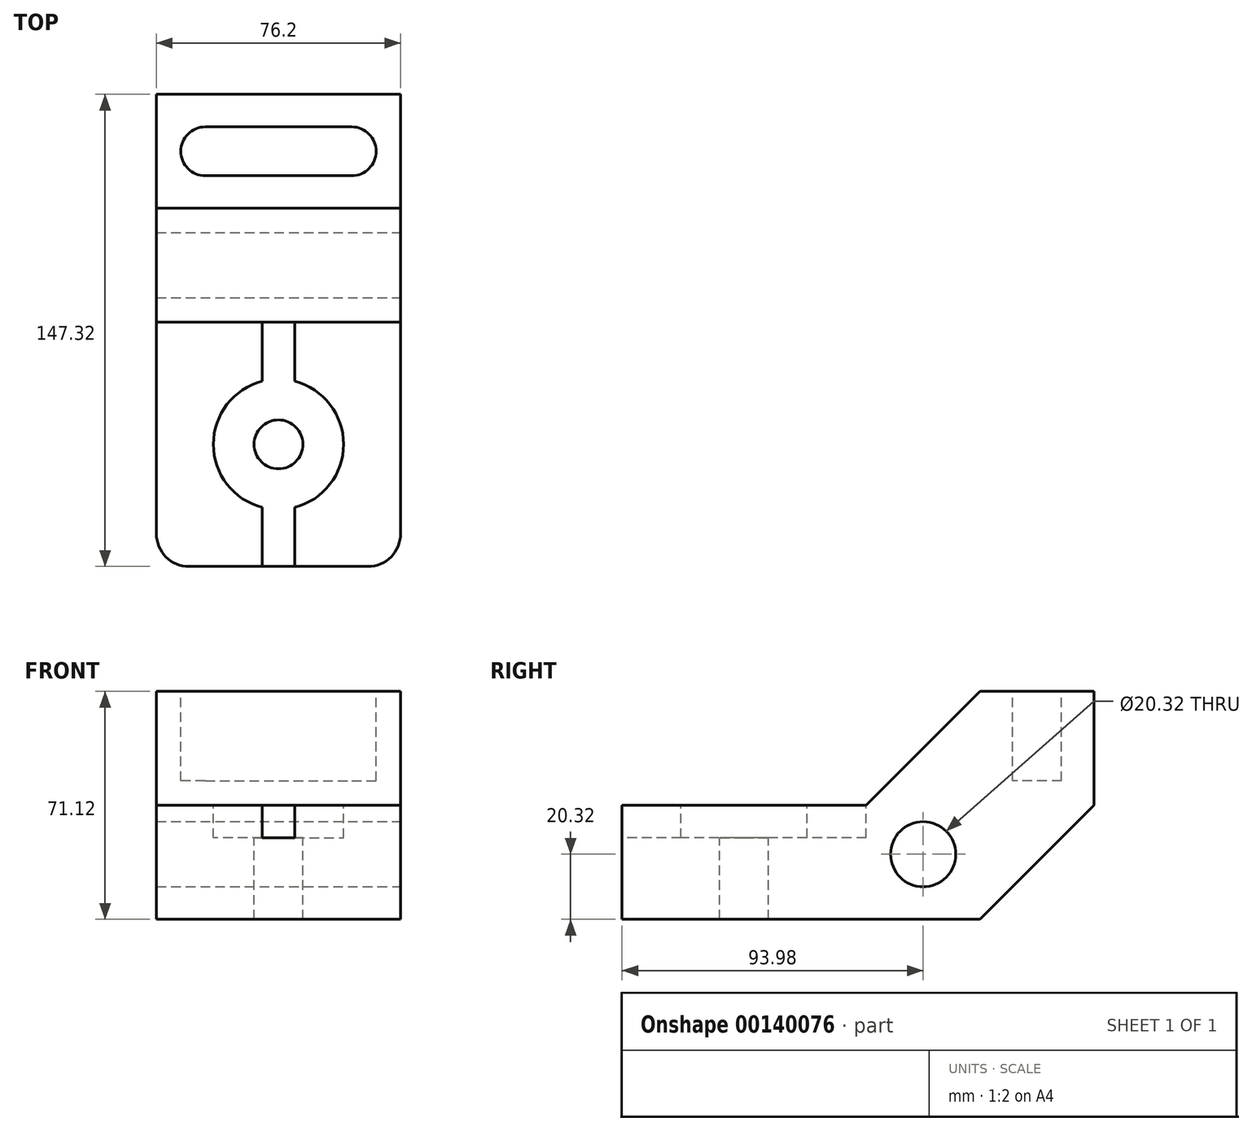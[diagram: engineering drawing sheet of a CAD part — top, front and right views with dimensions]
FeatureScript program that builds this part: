
annotation { "Feature Type Name" : "Feature", "Feature Type Description" : "" }
export const myFeature = defineFeature(function(context is Context, id is Id, definition is map)
    precondition{}
    {
        {
            var Q0;
            Q0=qCreatedBy(makeId("Right.planeOp"),FACE);
            var sketch = newSketch(context, id + "F0", { "sketchPlane" : qUnion([Q0])});
            skLineSegment(sketch, "E0", {"start": v(0, 0) * mm, "end": v(111.76, 0) * mm});
            skLineSegment(sketch, "E1", {"start": v(111.76, 0) * mm, "end": v(147.32, 35.56) * mm});
            skLineSegment(sketch, "E2", {"start": v(147.32, 35.56) * mm, "end": v(147.32, 71.12) * mm});
            skLineSegment(sketch, "E3", {"start": v(147.32, 71.12) * mm, "end": v(111.76, 71.12) * mm});
            skLineSegment(sketch, "E4", {"start": v(111.76, 71.12) * mm, "end": v(76.2, 35.56) * mm});
            skLineSegment(sketch, "E5", {"start": v(76.2, 35.56) * mm, "end": v(0, 35.56) * mm});
            skLineSegment(sketch, "E6", {"start": v(0, 35.56) * mm, "end": v(0, 0) * mm});
            skSolve(sketch);
        }
        {
            var Q0;
            Q0 = qSketchRegion(id + "F0", true);
            extrude(context, id + "F1", {"entities" : qUnion([Q0]), "endBound" : BoundingType.SYMMETRIC, "depth" : 76.2 * mm});
        }
        {
            var Q0;
            Q0=makeQuery(id+"F1.opExtrude","CAP_EDGE",EDGE,{"disambiguationData":[OSD([sQuery(id+"F0.wireOp",EDGE,"E6")])],"isStart":false});
            var Q1;
            Q1=makeQuery(id+"F1.opExtrude","CAP_EDGE",EDGE,{"disambiguationData":[OSD([sQuery(id+"F0.wireOp",EDGE,"E6")])],"isStart":true});
            fillet(context, id + "F2", {"entities" : qUnion([Q0, Q1]), "radius" : 10.16 * mm, "tangentPropagation" : true, "allowEdgeOverflow" : false});
        }
        {
            var Q0;
            Q0=makeQuery(id+"F1.opExtrude","CAP_FACE",FACE,{"disambiguationData":[OSD([sQuery(id+"F0.wireOp",EDGE,"E0"),sQuery(id+"F0.wireOp",EDGE,"E1"),sQuery(id+"F0.wireOp",EDGE,"E2"),sQuery(id+"F0.wireOp",EDGE,"E3"),sQuery(id+"F0.wireOp",EDGE,"E4"),sQuery(id+"F0.wireOp",EDGE,"E5"),sQuery(id+"F0.wireOp",EDGE,"E6")])],"isStart":false});
            var sketch = newSketch(context, id + "F3", { "sketchPlane" : qUnion([Q0])});
            skCircle(sketch, "E7", {"center": v(93.98, 20.32) * mm, "radius": 10.16 * mm});
            skSolve(sketch);
        }
        {
            var Q0;
            Q0 = qSketchRegion(id + "F3", true);
            extrude(context, id + "F4", {"entities" : qUnion([Q0]), "operationType" : NewBodyOperationType.REMOVE, "endBound" : BoundingType.THROUGH_ALL, "oppositeDirection" : true, "depth" : 25.4 * mm});
        }
        {
            var Q0;
            Q0=makeQuery(id+"F1.opExtrude","SWEPT_FACE",FACE,{"disambiguationData":[OSD([sQuery(id+"F0.wireOp",EDGE,"E3")])]});
            var sketch = newSketch(context, id + "F5", { "sketchPlane" : qUnion([Q0])});
            skLineSegment(sketch, "E8", {"start": v(-22.86, 121.92) * mm, "end": v(22.86, 121.92) * mm});
            skArc(sketch, "E9", {"start": v(22.86, 121.92) * mm, "mid": v(30.48, 129.54) * mm, "end": v(22.86, 137.16) * mm});
            skLineSegment(sketch, "E10", {"start": v(22.86, 137.16) * mm, "end": v(-22.86, 137.16) * mm});
            skArc(sketch, "E11", {"start": v(-22.86, 137.16) * mm, "mid": v(-30.48, 129.54) * mm, "end": v(-22.86, 121.92) * mm});
            skSolve(sketch);
        }
        {
            var Q0;
            Q0=makeQuery(id+"F1.opExtrude","SWEPT_FACE",FACE,{"disambiguationData":[OSD([sQuery(id+"F0.wireOp",EDGE,"E5")])]});
            var sketch = newSketch(context, id + "F6", { "sketchPlane" : qUnion([Q0])});
            skPoint(sketch, "E12", {"position": v(0, 38.1) * mm});
            skSolve(sketch);
        }
        {
            var Q0;
            Q0=sQuery(id+"F6.wireOp",VERTEX,"E12");
            var Q1;
            Q1=makeQuery(id+"F1.opExtrude","SWEPT_BODY",BODY,{"disambiguationData":[OSD([sQuery(id+"F0.wireOp",EDGE,"E0"),sQuery(id+"F0.wireOp",EDGE,"E1"),sQuery(id+"F0.wireOp",EDGE,"E2"),sQuery(id+"F0.wireOp",EDGE,"E3"),sQuery(id+"F0.wireOp",EDGE,"E4"),sQuery(id+"F0.wireOp",EDGE,"E5"),sQuery(id+"F0.wireOp",EDGE,"E6")])]});
            hole(context, id + "F7", {"style" : HoleStyle.C_BORE, "endStyle" : HoleEndStyle.THROUGH, "holeDiameter" : 15.24 * mm, "cBoreDiameter" : 40.64 * mm, "cBoreDepth" : 10.16 * mm, "locations" : qUnion([Q0]), "scope" : qUnion([Q1]), "isTappedThrough" : true});
        }
        {
            var Q0;
            Q0=makeQuery(id+"F1.opExtrude","SWEPT_FACE",FACE,{"disambiguationData":[OSD([sQuery(id+"F0.wireOp",EDGE,"E6")])]});
            var sketch = newSketch(context, id + "F8", { "sketchPlane" : qUnion([Q0])});
            skLineSegment(sketch, "E13", {"start": v(-5.08, 35.56) * mm, "end": v(-5.08, 25.4) * mm});
            skLineSegment(sketch, "E14", {"start": v(-5.08, 25.4) * mm, "end": v(5.08, 25.4) * mm});
            skLineSegment(sketch, "E15", {"start": v(5.08, 25.4) * mm, "end": v(5.08, 35.56) * mm});
            skLineSegment(sketch, "E16", {"start": v(5.08, 35.56) * mm, "end": v(-5.08, 35.56) * mm});
            skSolve(sketch);
        }
        {
            var Q0;
            Q0 = qSketchRegion(id + "F8", true);
            extrude(context, id + "F9", {"entities" : qUnion([Q0]), "operationType" : NewBodyOperationType.REMOVE, "oppositeDirection" : true, "depth" : 76.2 * mm});
        }
        {
            var Q0;
            Q0=makeQuery(id+"F5.imprint","IMPRINT",FACE,{"disambiguationData":[TD([[makeQuery(id+"F5.imprint","IMPRINT",EDGE,{"derivedFrom":sQuery(id+"F5.wireOp",EDGE,"E8")}),1.0]])]});
            extrude(context, id + "F10", {"entities" : qUnion([Q0]), "operationType" : NewBodyOperationType.REMOVE, "oppositeDirection" : true, "depth" : 27.94 * mm});
        }
    });
